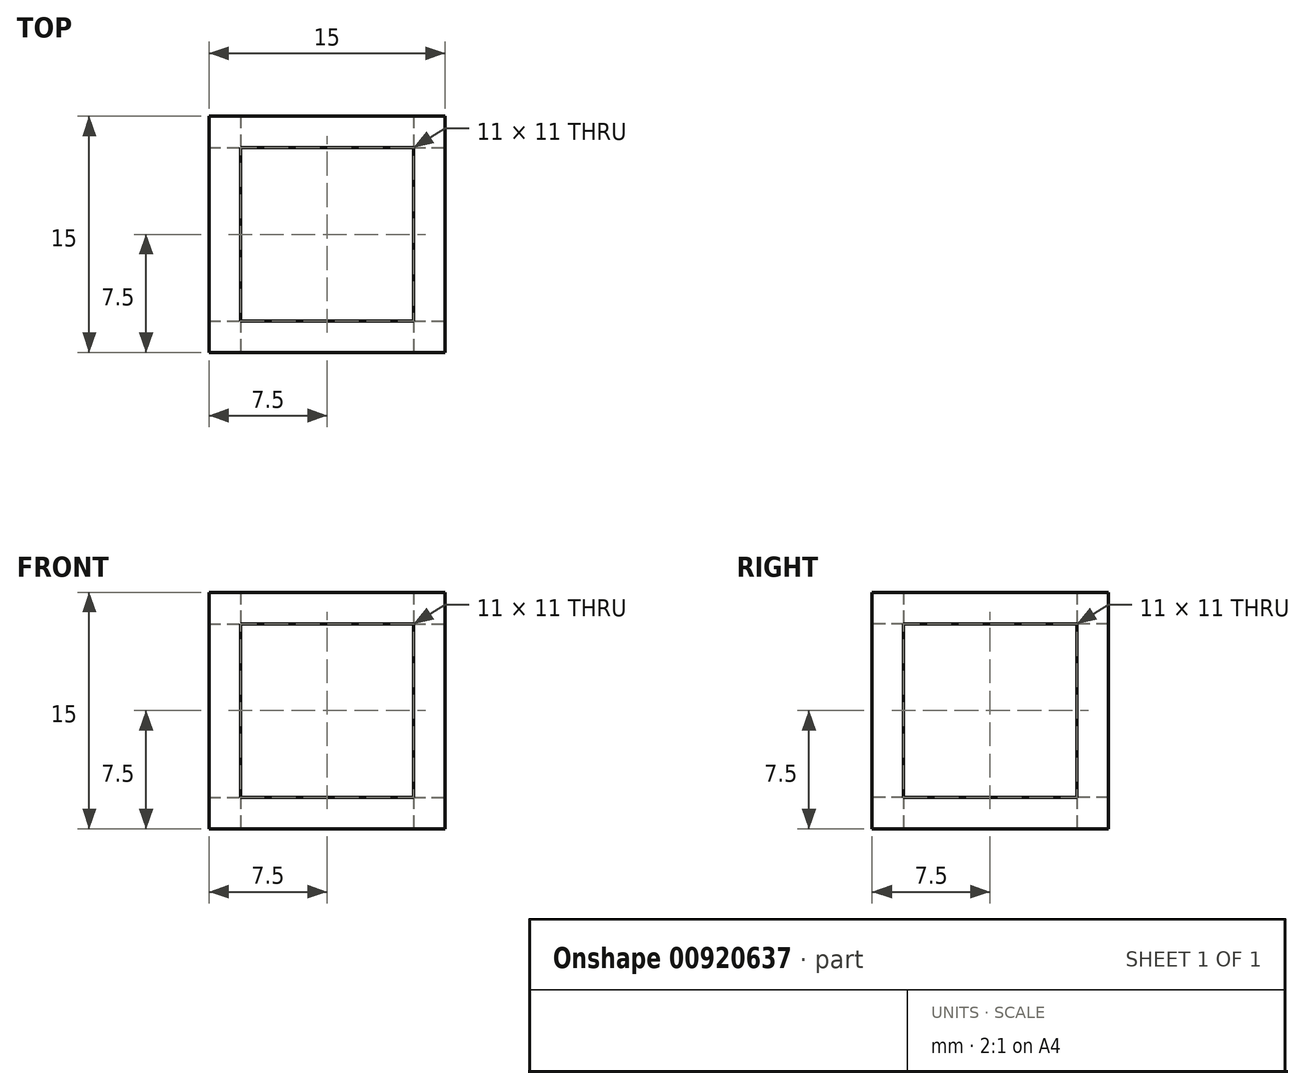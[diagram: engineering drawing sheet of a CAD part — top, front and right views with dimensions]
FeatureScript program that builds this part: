
annotation { "Feature Type Name" : "Feature", "Feature Type Description" : "" }
export const myFeature = defineFeature(function(context is Context, id is Id, definition is map)
    precondition{}
    {
        {
            var Q0;
            Q0=qCreatedBy(makeId("Top.planeOp"),FACE);
            var sketch = newSketch(context, id + "F0", { "sketchPlane" : qUnion([Q0])});
            skLineSegment(sketch, "E0.bottom", {"start": v(7.5, -7.5) * mm, "end": v(-7.5, -7.5) * mm});
            skLineSegment(sketch, "E0.top", {"start": v(7.5, 7.5) * mm, "end": v(-7.5, 7.5) * mm});
            skLineSegment(sketch, "E0.left", {"start": v(7.5, -7.5) * mm, "end": v(7.5, 7.5) * mm});
            skLineSegment(sketch, "E0.right", {"start": v(-7.5, -7.5) * mm, "end": v(-7.5, 7.5) * mm});
            skPoint(sketch, "E0.middle", {"position": v(0, 0) * mm});
            skLineSegment(sketch, "E1.bottom", {"start": v(5.5, -5.5) * mm, "end": v(-5.5, -5.5) * mm});
            skLineSegment(sketch, "E1.top", {"start": v(5.5, 5.5) * mm, "end": v(-5.5, 5.5) * mm});
            skLineSegment(sketch, "E1.left", {"start": v(5.5, -5.5) * mm, "end": v(5.5, 5.5) * mm});
            skLineSegment(sketch, "E1.right", {"start": v(-5.5, -5.5) * mm, "end": v(-5.5, 5.5) * mm});
            skSolve(sketch);
        }
        {
            var Q0;
            Q0=makeQuery(id+"F0.imprint","IMPRINT",FACE,{"disambiguationData":[TD([[makeQuery(id+"F0.imprint","IMPRINT",EDGE,{"derivedFrom":sQuery(id+"F0.wireOp",EDGE,"E0.bottom")}),-1.0]])]});
            extrude(context, id + "F1", {"entities" : qUnion([Q0]), "depth" : 7.5 * mm, "offsetDistance" : 25 * mm, "hasSecondDirection" : true, "secondDirectionOppositeDirection" : true, "secondDirectionDepth" : 7.5 * mm});
        }
        {
            var Q0;
            Q0=makeQuery(id+"F1.opExtrude","SWEPT_FACE",FACE,{"disambiguationData":[OSD([sQuery(id+"F0.wireOp",EDGE,"E0.bottom")])]});
            var sketch = newSketch(context, id + "F2", { "sketchPlane" : qUnion([Q0])});
            skLineSegment(sketch, "E2.bottom", {"start": v(5.5, -5.5) * mm, "end": v(-5.5, -5.5) * mm});
            skLineSegment(sketch, "E2.top", {"start": v(5.5, 5.5) * mm, "end": v(-5.5, 5.5) * mm});
            skLineSegment(sketch, "E2.left", {"start": v(5.5, -5.5) * mm, "end": v(5.5, 5.5) * mm});
            skLineSegment(sketch, "E2.right", {"start": v(-5.5, -5.5) * mm, "end": v(-5.5, 5.5) * mm});
            skPoint(sketch, "E2.middle", {"position": v(0, 0) * mm});
            skSolve(sketch);
        }
        {
            var Q0;
            Q0 = qSketchRegion(id + "F2", true);
            extrude(context, id + "F3", {"entities" : qUnion([Q0]), "operationType" : NewBodyOperationType.REMOVE, "oppositeDirection" : true, "depth" : 25 * mm, "offsetDistance" : 25 * mm});
        }
        {
            var Q0;
            Q0=makeQuery(id+"F1.opExtrude","SWEPT_FACE",FACE,{"disambiguationData":[OSD([sQuery(id+"F0.wireOp",EDGE,"E0.left")])]});
            var sketch = newSketch(context, id + "F4", { "sketchPlane" : qUnion([Q0])});
            skLineSegment(sketch, "E3.bottom", {"start": v(5.5, -5.5) * mm, "end": v(-5.5, -5.5) * mm});
            skLineSegment(sketch, "E3.top", {"start": v(5.5, 5.5) * mm, "end": v(-5.5, 5.5) * mm});
            skLineSegment(sketch, "E3.left", {"start": v(5.5, -5.5) * mm, "end": v(5.5, 5.5) * mm});
            skLineSegment(sketch, "E3.right", {"start": v(-5.5, -5.5) * mm, "end": v(-5.5, 5.5) * mm});
            skPoint(sketch, "E3.middle", {"position": v(0, 0) * mm});
            skSolve(sketch);
        }
        {
            var Q0;
            Q0 = qSketchRegion(id + "F4", true);
            extrude(context, id + "F5", {"entities" : qUnion([Q0]), "operationType" : NewBodyOperationType.REMOVE, "endBound" : BoundingType.THROUGH_ALL, "oppositeDirection" : true, "depth" : 25 * mm, "offsetDistance" : 25 * mm});
        }
        {
            var Q0;
            Q0=qCreatedBy(makeId("Top.planeOp"),FACE);
            var sketch = newSketch(context, id + "F6", { "sketchPlane" : qUnion([Q0])});
            skArc(sketch, "E4", {"start": v(7, 0) * mm, "mid": v(0, 7) * mm, "end": v(-7, 0) * mm});
            skLineSegment(sketch, "E5", {"start": v(0, 0) * mm, "end": v(26.22, 0) * mm, "construction": true});
            skLineSegment(sketch, "E6", {"start": v(0, 0) * mm, "end": v(-7, 0) * mm});
            skLineSegment(sketch, "E7", {"start": v(0, 0) * mm, "end": v(7, 0) * mm});
            skSolve(sketch);
        }
        {
            var Q0;
            Q0=sQuery(id+"F6.wireOp",EDGE,"E4");
            var Q1;
            Q1=sQuery(id+"F6.wireOp",EDGE,"E5");
            revolve(context, id + "F7", {"bodyType" : ToolBodyType.SURFACE, "surfaceOperationType" : NewSurfaceOperationType.NEW, "surfaceEntities" : qUnion([Q0]), "axis" : qUnion([Q1]), "revolveType" : RevolveType.FULL});
        }
    });
